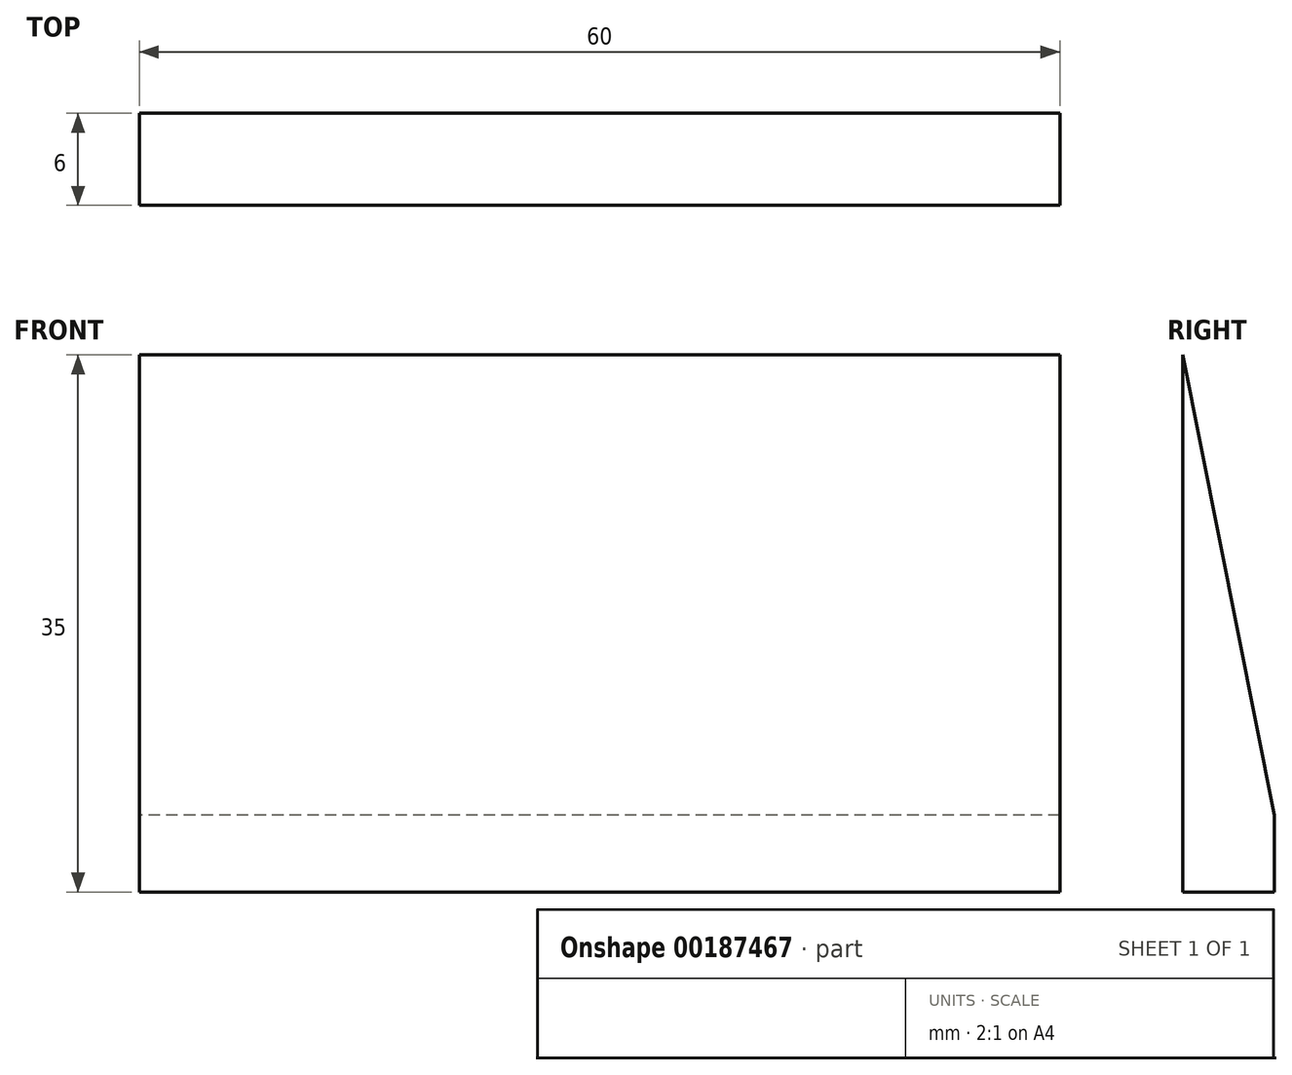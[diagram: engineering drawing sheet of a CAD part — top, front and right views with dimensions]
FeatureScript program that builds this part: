
annotation { "Feature Type Name" : "Feature", "Feature Type Description" : "" }
export const myFeature = defineFeature(function(context is Context, id is Id, definition is map)
    precondition{}
    {
        {
            var Q0;
            Q0=qCreatedBy(makeId("Right.planeOp"),FACE);
            var sketch = newSketch(context, id + "F0", { "sketchPlane" : qUnion([Q0])});
            skLineSegment(sketch, "E0", {"start": v(0, 0) * mm, "end": v(6, 0) * mm});
            skLineSegment(sketch, "E1", {"start": v(6, 0) * mm, "end": v(6, 5) * mm});
            skLineSegment(sketch, "E2", {"start": v(0, 0) * mm, "end": v(0, 35) * mm});
            skLineSegment(sketch, "E3", {"start": v(0, 35) * mm, "end": v(6, 5) * mm});
            skSolve(sketch);
        }
        {
            var Q0;
            Q0 = qSketchRegion(id + "F0", true);
            extrude(context, id + "F1", {"entities" : qUnion([Q0]), "depth" : 60 * mm});
        }
    });
